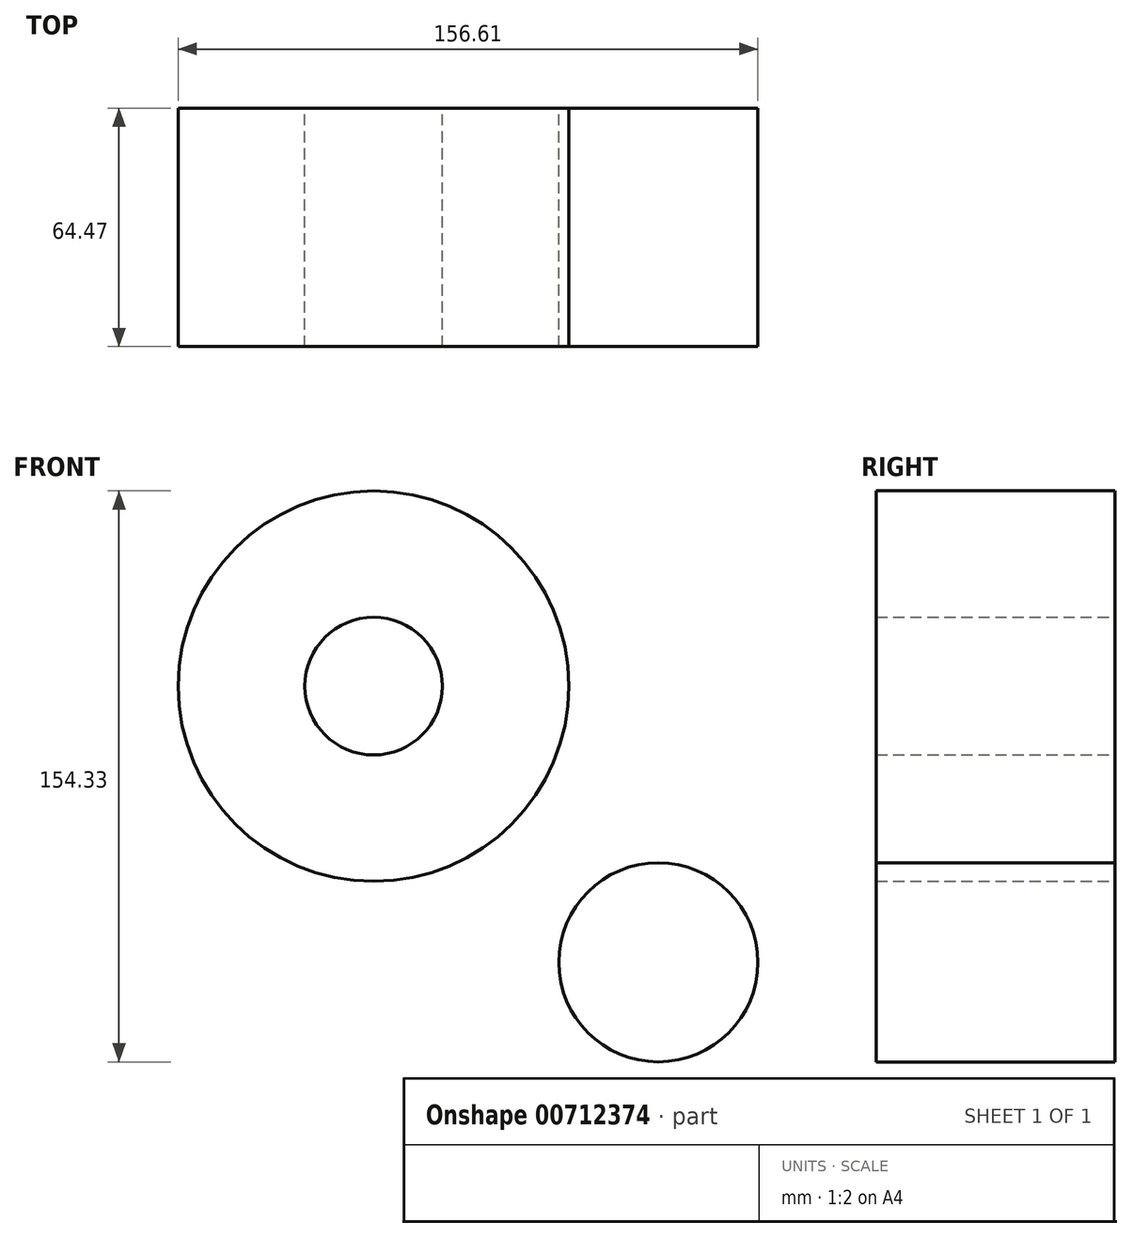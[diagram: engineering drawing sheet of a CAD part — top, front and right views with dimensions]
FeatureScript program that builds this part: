
annotation { "Feature Type Name" : "Feature", "Feature Type Description" : "" }
export const myFeature = defineFeature(function(context is Context, id is Id, definition is map)
    precondition{}
    {
        {
            var Q0;
            Q0=qCreatedBy(makeId("Front.planeOp"),FACE);
            var sketch = newSketch(context, id + "F0", { "sketchPlane" : qUnion([Q0])});
            skCircle(sketch, "E0", {"center": v(0, 0) * mm, "radius": 52.77 * mm});
            skSolve(sketch);
        }
        {
            var Q0;
            Q0=makeQuery(id+"F0.imprint","IMPRINT",FACE,{"disambiguationData":[TD([[makeQuery(id+"F0.imprint","IMPRINT",EDGE,{"derivedFrom":sQuery(id+"F0.wireOp",EDGE,"E0")}),1.0]])]});
            var sketch = newSketch(context, id + "F1", { "sketchPlane" : qUnion([Q0])});
            skCircle(sketch, "E1", {"center": v(0, 0) * mm, "radius": 18.6 * mm});
            skSolve(sketch);
        }
        {
            var Q0;
            Q0=qCreatedBy(makeId("Front.planeOp"),FACE);
            var sketch = newSketch(context, id + "F2", { "sketchPlane" : qUnion([Q0])});
            skCircle(sketch, "E2", {"center": v(76.94, -74.65) * mm, "radius": 26.9 * mm});
            skSolve(sketch);
        }
        {
            var Q0;
            Q0=qCreatedBy(makeId("Front.planeOp"),FACE);
            var sketch = newSketch(context, id + "F3", { "sketchPlane" : qUnion([Q0])});
            skLineSegment(sketch, "E3", {"start": v(0, -8.08) * mm, "end": v(75.65, -77.4) * mm});
            skLineSegment(sketch, "E4", {"start": v(75.65, -77.4) * mm, "end": v(24.35, 41.13) * mm});
            skSolve(sketch);
        }
        {
            var Q0;
            Q0 = qSketchRegion(id + "F2", true);
            var Q1;
            Q1 = qSketchRegion(id + "F1", true);
            var Q2;
            Q2 = qSketchRegion(id + "F3", true);
            var Q3;
            Q3=makeQuery(id+"F0.imprint","IMPRINT",FACE,{"disambiguationData":[TD([[makeQuery(id+"F0.imprint","IMPRINT",EDGE,{"derivedFrom":sQuery(id+"F0.wireOp",EDGE,"E0")}),1.0]])]});
            extrude(context, id + "F4", {"entities" : qUnion([Q0, Q1, Q2, Q3]), "depth" : 64.47 * mm, "offsetDistance" : 25.4 * mm});
        }
    });
